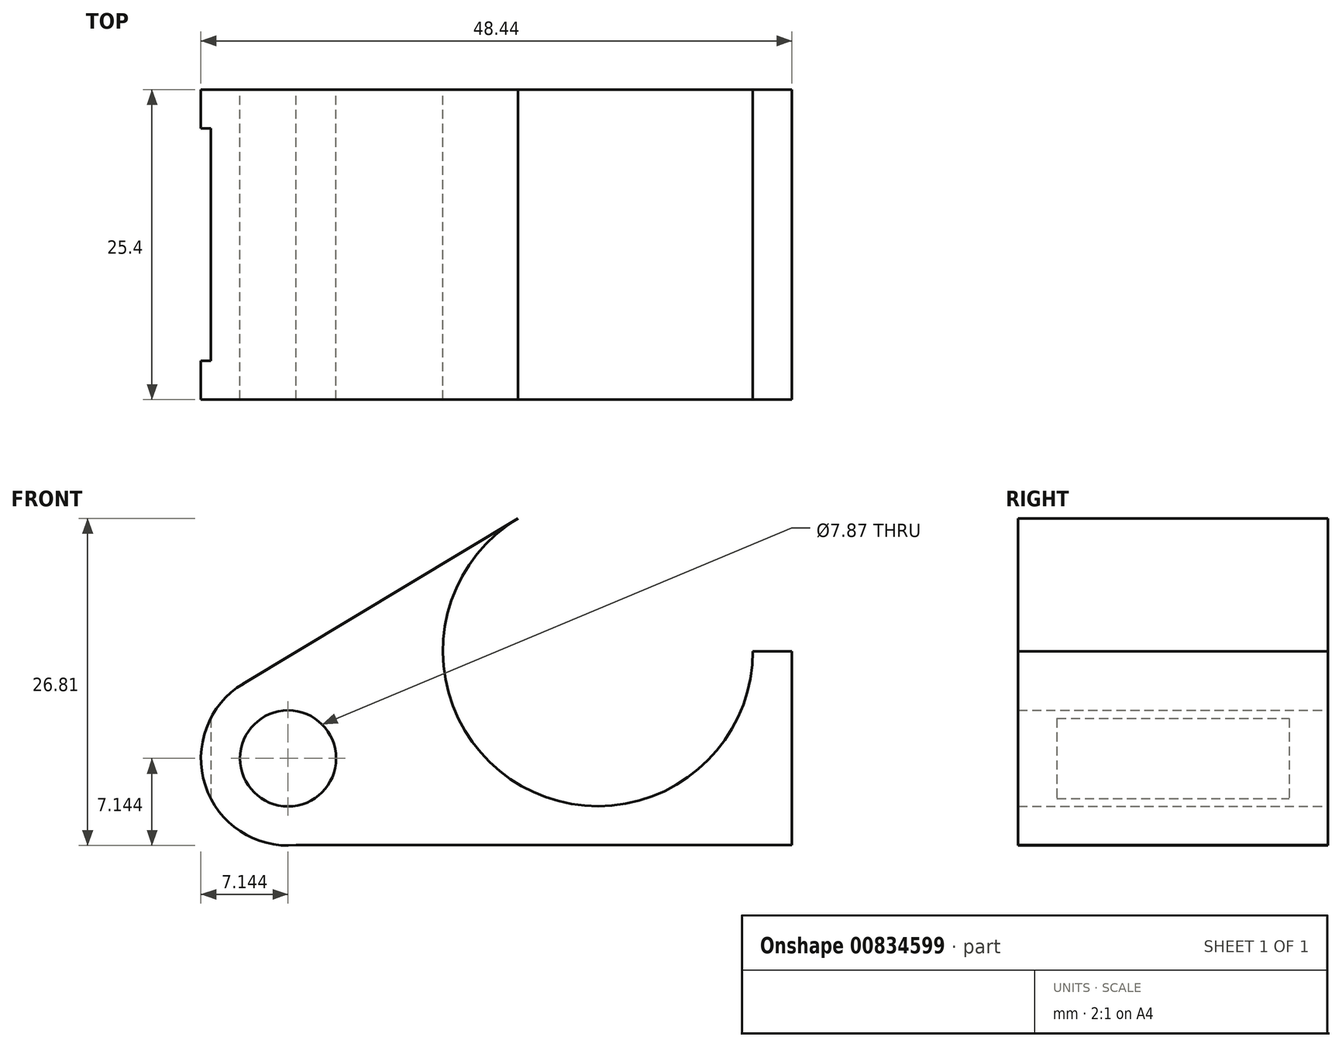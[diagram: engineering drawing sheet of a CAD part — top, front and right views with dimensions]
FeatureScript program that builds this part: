
annotation { "Feature Type Name" : "Feature", "Feature Type Description" : "" }
export const myFeature = defineFeature(function(context is Context, id is Id, definition is map)
    precondition{}
    {
        {
            var Q0;
            Q0=qCreatedBy(makeId("Front.planeOp"),FACE);
            var sketch = newSketch(context, id + "F0", { "sketchPlane" : qUnion([Q0])});
            skArc(sketch, "E0", {"start": v(599.71, 54.5) * mm, "mid": v(596.6, 46.16) * mm, "end": v(604.03, 41.26) * mm});
            skPoint(sketch, "E1.start.orphan", {"position": v(596.25, 48.37) * mm});
            skLineSegment(sketch, "E2", {"start": v(599.71, 54.5) * mm, "end": v(622.24, 68.04) * mm});
            skLineSegment(sketch, "E3", {"start": v(602.75, 41.26) * mm, "end": v(628.79, 41.26) * mm});
            skLineSegment(sketch, "E4", {"start": v(641.49, 57.16) * mm, "end": v(644.69, 57.16) * mm});
            skPoint(sketch, "E5", {"position": v(622.24, 68.04) * mm});
            skPoint(sketch, "E6", {"position": v(641.49, 57.16) * mm});
            skArc(sketch, "E7", {"start": v(622.24, 68.04) * mm, "mid": v(622.55, 46.1) * mm, "end": v(641.49, 57.19) * mm});
            skLineSegment(sketch, "E8", {"start": v(644.69, 57.16) * mm, "end": v(644.69, 41.26) * mm});
            skLineSegment(sketch, "E9", {"start": v(628.79, 41.26) * mm, "end": v(644.69, 41.26) * mm});
            skLineSegment(sketch, "E10", {"start": v(608.32, 67.75) * mm, "end": v(617.22, 42.03) * mm, "construction": true});
            skLineSegment(sketch, "E11", {"start": v(628.79, 57.16) * mm, "end": v(598.48, 57.58) * mm, "construction": true});
            skLineSegment(sketch, "E12", {"start": v(598.48, 57.58) * mm, "end": v(603.4, 48.37) * mm, "construction": true});
            skLineSegment(sketch, "E13", {"start": v(628.79, 57.16) * mm, "end": v(603.4, 48.37) * mm, "construction": true});
            skSolve(sketch);
        }
        {
            var Q0;
            Q0 = qSketchRegion(id + "F0", true);
            extrude(context, id + "F1", {"entities" : qUnion([Q0]), "depth" : 12.7 * mm, "offsetDistance" : 25.4 * mm, "hasSecondDirection" : true, "secondDirectionOppositeDirection" : true, "secondDirectionDepth" : 12.7 * mm});
        }
        {
            var Q0;
            Q0=makeQuery(id+"F1.opExtrude","CAP_FACE",FACE,{"disambiguationData":[OSD([sQuery(id+"F0.wireOp",EDGE,"E0"),sQuery(id+"F0.wireOp",EDGE,"E2"),sQuery(id+"F0.wireOp",EDGE,"E3"),sQuery(id+"F0.wireOp",EDGE,"E4"),sQuery(id+"F0.wireOp",EDGE,"E7"),sQuery(id+"F0.wireOp",EDGE,"E8"),sQuery(id+"F0.wireOp",EDGE,"E9")])],"isStart":true});
            var sketch = newSketch(context, id + "F2", { "sketchPlane" : qUnion([Q0])});
            skCircle(sketch, "E14", {"center": v(-603.4, 48.37) * mm, "radius": 3.94 * mm});
            skSolve(sketch);
        }
        {
            var Q0;
            Q0 = qSketchRegion(id + "F2", true);
            extrude(context, id + "F3", {"entities" : qUnion([Q0]), "operationType" : NewBodyOperationType.REMOVE, "endBound" : BoundingType.THROUGH_ALL, "oppositeDirection" : true, "depth" : 25.4 * mm, "offsetDistance" : 25.4 * mm});
        }
        {
            var Q0;
            Q0=makeQuery(id+"F3.boolean.opBoolean","COPY",EDGE,{"derivedFrom":makeQuery(id+"F3.opExtrude","CAP_EDGE",EDGE,{"disambiguationData":[OSD([sQuery(id+"F2.wireOp",EDGE,"E14")])],"isStart":true})});
            var Q1;
            Q1=makeQuery(id+"F1.opExtrude","CAP_EDGE",EDGE,{"disambiguationData":[OSD([sQuery(id+"F0.wireOp",EDGE,"E7")])],"isStart":true});
            cPlane(context, id + "F4", {"entities" : qUnion([Q0, Q1]), "cplaneType" : CPlaneType.LINE_ANGLE, "offset" : 25.4 * mm, "angle" : 0 * degree, "width" : 152.4 * mm, "height" : 152.4 * mm});
        }
        {
            var Q0;
            Q0=qCreatedBy(id+"F4.planeOp",FACE);
            var sketch = newSketch(context, id + "F5", { "sketchPlane" : qUnion([Q0])});
            skLineSegment(sketch, "E15.bottom", {"start": v(597.05, 9.53) * mm, "end": v(571.62, 9.52) * mm});
            skLineSegment(sketch, "E15.top", {"start": v(597.05, -9.52) * mm, "end": v(571.62, -9.53) * mm});
            skLineSegment(sketch, "E15.left", {"start": v(597.05, 9.53) * mm, "end": v(597.05, -9.52) * mm});
            skLineSegment(sketch, "E15.right", {"start": v(571.62, 9.53) * mm, "end": v(571.62, -9.53) * mm});
            skPoint(sketch, "E16", {"position": v(600.22, 0) * mm});
            skSolve(sketch);
        }
        {
            var Q0;
            Q0 = qSketchRegion(id + "F5", true);
            extrude(context, id + "F6", {"entities" : qUnion([Q0]), "operationType" : NewBodyOperationType.REMOVE, "endBound" : BoundingType.THROUGH_ALL, "oppositeDirection" : true, "depth" : 25.4 * mm, "offsetDistance" : 25.4 * mm, "hasSecondDirection" : true, "secondDirectionBound" : SecondDirectionBoundingType.THROUGH_ALL, "secondDirectionOppositeDirection" : false, "secondDirectionDepth" : 25.4 * mm});
        }
    });
